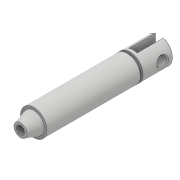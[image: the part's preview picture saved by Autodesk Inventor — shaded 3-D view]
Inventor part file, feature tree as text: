
AUTODESK INVENTOR PART (.ipt)
format: ipt  version: 2018.1 (Build 221171000, 171)  size: 158,720 bytes
history: native  units: mm
features: hole x2, chamfer x2, sketch x2, other x1, revolve x1, extrude x1
ambient origin geometry x8: Origin, YZ Plane, XZ Plane, XY Plane, X Axis, Y Axis, Z Axis, Center Point
bodies: Body1 (feature_tree)
feature tree (9):
  other  "Твердое тело1"
  revolve  "Вращение1"
  hole  "Отверстие1"  [1 undecoded]
  chamfer  "Фаска1"  Distance=42.0mm
  extrude  "Выдавливание1"  Depth=8.0mm
  hole  "Отверстие2"  [1 undecoded]
  chamfer  "Фаска2"  Distance=2.0mm
  sketch  "Эскиз1"
  sketch  "Эскиз2"
note: 2 required parameter values undecoded (feature->parameter linkage not recoverable at this tier; creation-order binding heuristic only, values carry confidence <= 0.55)
